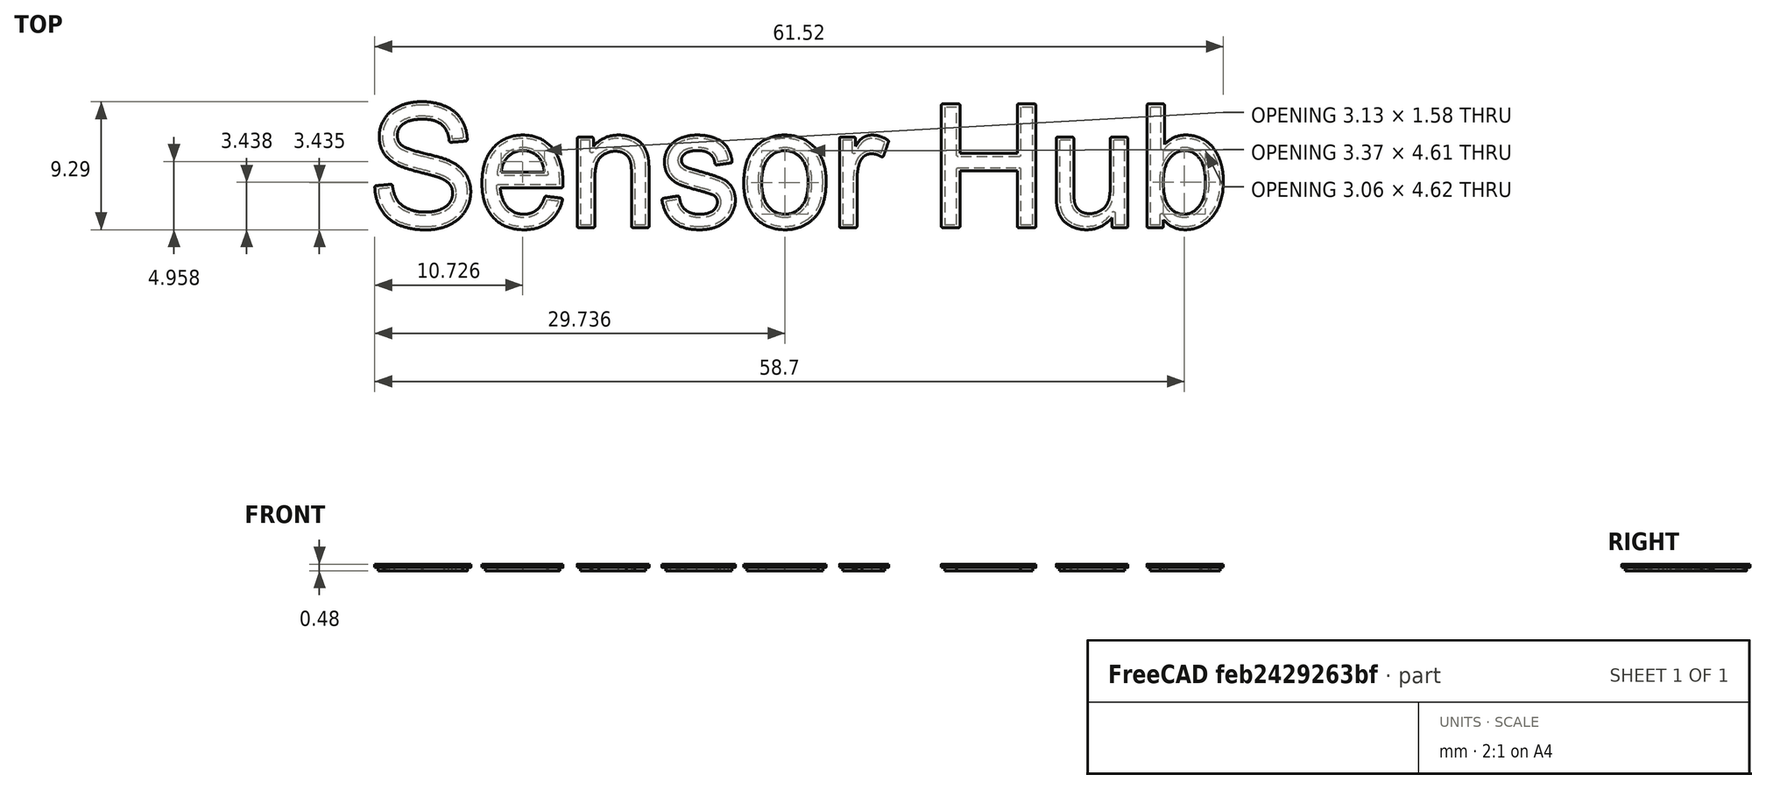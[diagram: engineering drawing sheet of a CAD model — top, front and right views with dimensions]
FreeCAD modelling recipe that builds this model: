
FCSTD DOCUMENT  (FreeCAD 0.21R33771 (Git))
Label: Label
License: Creative Commons Attribution-ShareAlike 4.0
LicenseURL: https://creativecommons.org/licenses/by-sa/4.0/
objects: Part::Feature×24, Part::Extrusion×24, Part::Cut×6, Part::MultiFuse×3
note: 57 computed .brp shape members not serialized (recipe doc carries the construction recipe); baked Part::Feature solids carry a one-line shape summary decoded from their .brp

FEATURE [Part::Feature] text113
  shape: bbox 6.96 x 9.293 x 2.036e-07 mm, 0 faces, 0 solids (baked)
FEATURE [Part::Feature] text113001
  shape: bbox 6.859 x 8.995 x 2.036e-07 mm, 0 faces, 0 solids (baked)
FEATURE [Part::Feature] text113002
  shape: bbox 5.539 x 9.138 x 2.036e-07 mm, 0 faces, 0 solids (baked)
FEATURE [Part::Feature] text113003
  shape: bbox 5.875 x 6.869 x 2.036e-07 mm, 0 faces, 0 solids (baked)
FEATURE [Part::Feature] text113004
  shape: bbox 5.207 x 6.726 x 2.036e-07 mm, 0 faces, 0 solids (baked)
FEATURE [Part::Feature] text113005
  shape: bbox 5.327 x 6.869 x 2.036e-07 mm, 0 faces, 0 solids (baked)
FEATURE [Part::Feature] text113006
  shape: bbox 5.965 x 6.869 x 2.036e-07 mm, 0 faces, 0 solids (baked)
FEATURE [Part::Feature] text113007
  shape: bbox 3.569 x 6.726 x 2.036e-07 mm, 0 faces, 0 solids (baked)
FEATURE [Part::Feature] text113008
  shape: bbox 5.194 x 6.726 x 2.036e-07 mm, 0 faces, 0 solids (baked)
FEATURE [Part::Feature] text113009
  shape: bbox 3.129 x 1.579 x 2.036e-07 mm, 0 faces, 0 solids (baked)
FEATURE [Part::Feature] text113010
  shape: bbox 3.062 x 4.619 x 2.036e-07 mm, 0 faces, 0 solids (baked)
FEATURE [Part::Feature] text113011
  shape: bbox 3.367 x 4.613 x 2.036e-07 mm, 0 faces, 0 solids (baked)
FEATURE [Part::Extrusion] Extrude
  Base = -> text113
  Dir = (0,0,1)
  DirMode = 0
  FaceMakerClass = Part::FaceMakerBullseye
  LengthFwd = 0.24
  LengthRev = 0
  Solid = true
  Symmetric = false
FEATURE [Part::Extrusion] Extrude001
  Base = -> text113001
  Dir = (0,0,1)
  DirMode = 0
  FaceMakerClass = Part::FaceMakerBullseye
  LengthFwd = 0.24
  LengthRev = 0
  Solid = true
  Symmetric = false
FEATURE [Part::Extrusion] Extrude002
  Base = -> text113002
  Dir = (0,0,1)
  DirMode = 0
  FaceMakerClass = Part::FaceMakerBullseye
  LengthFwd = 0.24
  LengthRev = 0
  Solid = true
  Symmetric = false
FEATURE [Part::Extrusion] Extrude003
  Base = -> text113003
  Dir = (0,0,1)
  DirMode = 0
  FaceMakerClass = Part::FaceMakerBullseye
  LengthFwd = 0.24
  LengthRev = 0
  Solid = true
  Symmetric = false
FEATURE [Part::Extrusion] Extrude004
  Base = -> text113004
  Dir = (0,0,1)
  DirMode = 0
  FaceMakerClass = Part::FaceMakerBullseye
  LengthFwd = 0.24
  LengthRev = 0
  Solid = true
  Symmetric = false
FEATURE [Part::Extrusion] Extrude005
  Base = -> text113005
  Dir = (0,0,1)
  DirMode = 0
  FaceMakerClass = Part::FaceMakerBullseye
  LengthFwd = 0.24
  LengthRev = 0
  Solid = true
  Symmetric = false
FEATURE [Part::Extrusion] Extrude006
  Base = -> text113006
  Dir = (0,0,1)
  DirMode = 0
  FaceMakerClass = Part::FaceMakerBullseye
  LengthFwd = 0.24
  LengthRev = 0
  Solid = true
  Symmetric = false
FEATURE [Part::Extrusion] Extrude007
  Base = -> text113007
  Dir = (0,0,1)
  DirMode = 0
  FaceMakerClass = Part::FaceMakerBullseye
  LengthFwd = 0.24
  LengthRev = 0
  Solid = true
  Symmetric = false
FEATURE [Part::Extrusion] Extrude008
  Base = -> text113008
  Dir = (0,0,1)
  DirMode = 0
  FaceMakerClass = Part::FaceMakerBullseye
  LengthFwd = 0.24
  LengthRev = 0
  Solid = true
  Symmetric = false
FEATURE [Part::Extrusion] Extrude009
  Base = -> text113009
  Dir = (0,0,1)
  DirMode = 0
  FaceMakerClass = Part::FaceMakerBullseye
  LengthFwd = 0.24
  LengthRev = 0
  Solid = true
  Symmetric = false
FEATURE [Part::Extrusion] Extrude010
  Base = -> text113010
  Dir = (0,0,1)
  DirMode = 0
  FaceMakerClass = Part::FaceMakerBullseye
  LengthFwd = 0.24
  LengthRev = 0
  Solid = true
  Symmetric = false
FEATURE [Part::Extrusion] Extrude011
  Base = -> text113011
  Dir = (0,0,1)
  DirMode = 0
  FaceMakerClass = Part::FaceMakerBullseye
  LengthFwd = 0.24
  LengthRev = 0
  Solid = true
  Symmetric = false
FEATURE [Part::Cut] Cut
  Base = -> Extrude003
  Tool = -> Extrude009
FEATURE [Part::Cut] Cut001
  Base = -> Extrude006
  Tool = -> Extrude011
FEATURE [Part::Cut] Cut002
  Base = -> Extrude002
  Tool = -> Extrude010
FEATURE [Part::MultiFuse] Fusion  label="Thick"
  Shapes = -> [Extrude,Extrude001,Extrude004,Extrude005,Extrude007,Extrude008,Cut,Cut001,Cut002]
FEATURE [Part::Feature] text113012
  shape: bbox 6.472 x 8.808 x 2.036e-07 mm, 1 faces, 0 solids (baked)
FEATURE [Part::Feature] text113013
  shape: bbox 6.391 x 8.51 x 2.036e-07 mm, 1 faces, 0 solids (baked)
FEATURE [Part::Feature] text113014
  shape: bbox 5.071 x 8.653 x 2.036e-07 mm, 1 faces, 0 solids (baked)
FEATURE [Part::Feature] text113015
  shape: bbox 5.407 x 6.384 x 2.036e-07 mm, 1 faces, 0 solids (baked)
FEATURE [Part::Feature] text113016
  shape: bbox 4.739 x 6.241 x 2.036e-07 mm, 1 faces, 0 solids (baked)
FEATURE [Part::Feature] text113017
  shape: bbox 4.818 x 6.384 x 2.036e-07 mm, 1 faces, 0 solids (baked)
FEATURE [Part::Feature] text113018
  shape: bbox 5.497 x 6.384 x 2.036e-07 mm, 1 faces, 0 solids (baked)
FEATURE [Part::Feature] text113019
  shape: bbox 3.058 x 6.241 x 2.036e-07 mm, 1 faces, 0 solids (baked)
FEATURE [Part::Feature] text113020
  shape: bbox 4.726 x 6.241 x 2.036e-07 mm, 1 faces, 0 solids (baked)
FEATURE [Part::Feature] text113021
  shape: bbox 3.65 x 2.064 x 2.036e-07 mm, 1 faces, 0 solids (baked)
FEATURE [Part::Feature] text113022
  shape: bbox 3.53 x 5.104 x 2.036e-07 mm, 1 faces, 0 solids (baked)
FEATURE [Part::Feature] text113023
  shape: bbox 3.835 x 5.098 x 2.036e-07 mm, 1 faces, 0 solids (baked)
FEATURE [Part::Extrusion] Extrude012
  Base = -> text113012
  Dir = (0,0,1)
  DirMode = 0
  FaceMakerClass = Part::FaceMakerBullseye
  LengthFwd = 0.24
  LengthRev = 0
  Solid = false
  Symmetric = false
FEATURE [Part::Extrusion] Extrude013
  Base = -> text113013
  Dir = (0,0,1)
  DirMode = 0
  FaceMakerClass = Part::FaceMakerBullseye
  LengthFwd = 0.24
  LengthRev = 0
  Solid = false
  Symmetric = false
FEATURE [Part::Extrusion] Extrude014
  Base = -> text113014
  Dir = (0,0,1)
  DirMode = 0
  FaceMakerClass = Part::FaceMakerBullseye
  LengthFwd = 0.24
  LengthRev = 0
  Solid = false
  Symmetric = false
FEATURE [Part::Extrusion] Extrude015
  Base = -> text113015
  Dir = (0,0,1)
  DirMode = 0
  FaceMakerClass = Part::FaceMakerBullseye
  LengthFwd = 0.24
  LengthRev = 0
  Solid = false
  Symmetric = false
FEATURE [Part::Extrusion] Extrude016
  Base = -> text113016
  Dir = (0,0,1)
  DirMode = 0
  FaceMakerClass = Part::FaceMakerBullseye
  LengthFwd = 0.24
  LengthRev = 0
  Solid = false
  Symmetric = false
FEATURE [Part::Extrusion] Extrude017
  Base = -> text113017
  Dir = (0,0,1)
  DirMode = 0
  FaceMakerClass = Part::FaceMakerBullseye
  LengthFwd = 0.24
  LengthRev = 0
  Solid = false
  Symmetric = false
FEATURE [Part::Extrusion] Extrude018
  Base = -> text113018
  Dir = (0,0,1)
  DirMode = 0
  FaceMakerClass = Part::FaceMakerBullseye
  LengthFwd = 0.24
  LengthRev = 0
  Solid = false
  Symmetric = false
FEATURE [Part::Extrusion] Extrude019
  Base = -> text113019
  Dir = (0,0,1)
  DirMode = 0
  FaceMakerClass = Part::FaceMakerBullseye
  LengthFwd = 0.24
  LengthRev = 0
  Solid = false
  Symmetric = false
FEATURE [Part::Extrusion] Extrude020
  Base = -> text113020
  Dir = (0,0,1)
  DirMode = 0
  FaceMakerClass = Part::FaceMakerBullseye
  LengthFwd = 0.24
  LengthRev = 0
  Solid = false
  Symmetric = false
FEATURE [Part::Extrusion] Extrude021
  Base = -> text113021
  Dir = (0,0,1)
  DirMode = 0
  FaceMakerClass = Part::FaceMakerBullseye
  LengthFwd = 0.24
  LengthRev = 0
  Solid = false
  Symmetric = false
FEATURE [Part::Extrusion] Extrude022
  Base = -> text113022
  Dir = (0,0,1)
  DirMode = 0
  FaceMakerClass = Part::FaceMakerBullseye
  LengthFwd = 0.24
  LengthRev = 0
  Solid = false
  Symmetric = false
FEATURE [Part::Extrusion] Extrude023
  Base = -> text113023
  Dir = (0,0,1)
  DirMode = 0
  FaceMakerClass = Part::FaceMakerBullseye
  LengthFwd = 0.24
  LengthRev = 0
  Solid = false
  Symmetric = false
FEATURE [Part::Cut] Cut003
  Base = -> Extrude015
  Tool = -> Extrude021
FEATURE [Part::Cut] Cut004
  Base = -> Extrude018
  Tool = -> Extrude023
FEATURE [Part::Cut] Cut005
  Base = -> Extrude014
  Tool = -> Extrude022
FEATURE [Part::MultiFuse] Fusion001  label="Thin"
  Placement = pos=(0,0,-0.24) rot=(0,0,1;0rad)
  Shapes = -> [Cut005,Extrude012,Extrude013,Extrude016,Extrude017,Extrude019,Extrude020,Cut003,Cut004]
FEATURE [Part::MultiFuse] Fusion002  label="SensorHub"
  Shapes = -> [Fusion,Fusion001]
